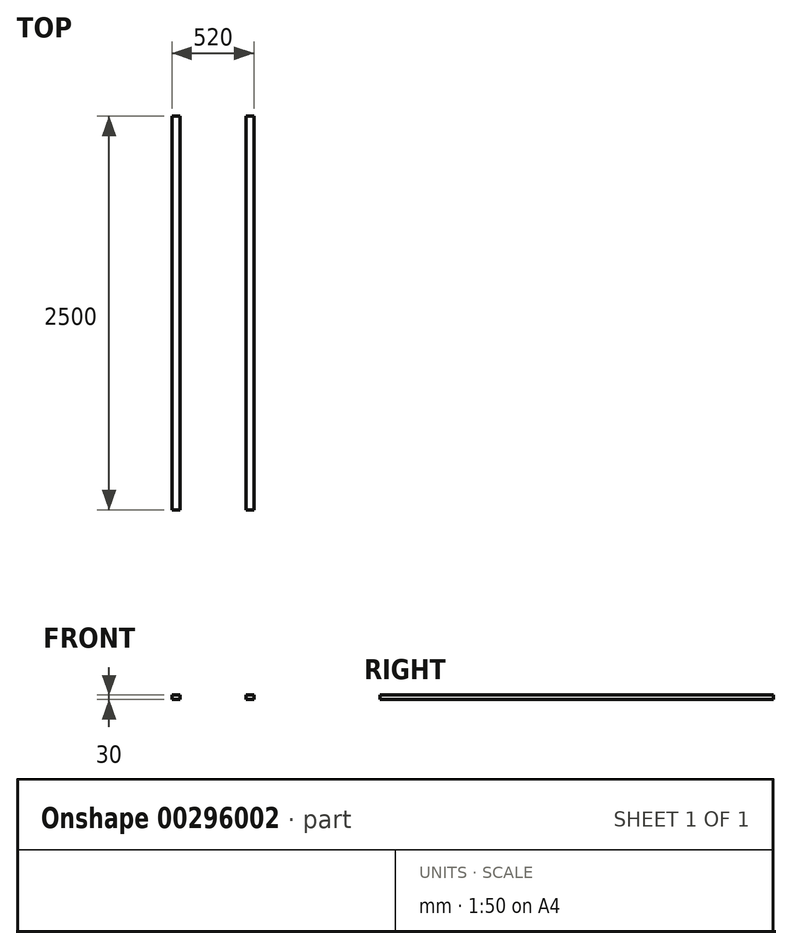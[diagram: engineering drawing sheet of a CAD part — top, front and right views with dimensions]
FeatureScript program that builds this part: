
annotation { "Feature Type Name" : "Feature", "Feature Type Description" : "" }
export const myFeature = defineFeature(function(context is Context, id is Id, definition is map)
    precondition{}
    {
        {
            var Q0;
            Q0=qCreatedBy(makeId("Top.planeOp"),FACE);
            var sketch = newSketch(context, id + "F0", { "sketchPlane" : qUnion([Q0])});
            skLineSegment(sketch, "E0.bottom", {"start": v(0, 0) * mm, "end": v(50, 0) * mm});
            skLineSegment(sketch, "E0.top", {"start": v(0, 2500) * mm, "end": v(50, 2500) * mm});
            skLineSegment(sketch, "E0.left", {"start": v(0, 0) * mm, "end": v(0, 2500) * mm});
            skLineSegment(sketch, "E0.right", {"start": v(50, 0) * mm, "end": v(50, 2500) * mm});
            skLineSegment(sketch, "E1.bottom", {"start": v(-420, 0) * mm, "end": v(-470, 0) * mm});
            skLineSegment(sketch, "E1.top", {"start": v(-420, 2500) * mm, "end": v(-470, 2500) * mm});
            skLineSegment(sketch, "E1.left", {"start": v(-470, 0) * mm, "end": v(-470, 2500) * mm});
            skLineSegment(sketch, "E1.right", {"start": v(-420, 0) * mm, "end": v(-420, 2500) * mm});
            skSolve(sketch);
        }
        {
            var Q0;
            Q0 = qSketchRegion(id + "F0", true);
            extrude(context, id + "F1", {"entities" : qUnion([Q0]), "depth" : 30 * mm});
        }
    });
